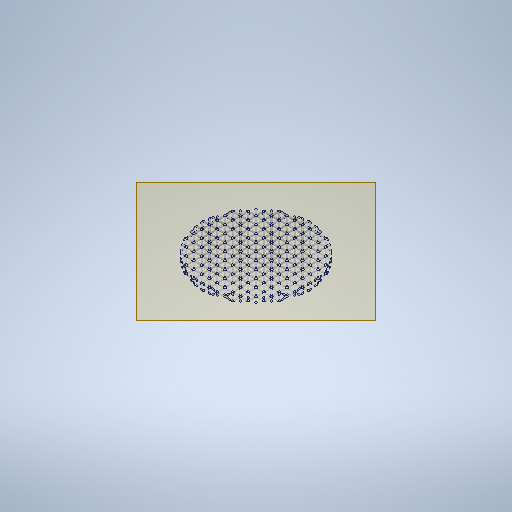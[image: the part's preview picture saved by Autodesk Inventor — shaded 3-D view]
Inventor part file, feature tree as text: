
AUTODESK INVENTOR PART (.ipt)
format: ipt  version: 2025.3 (Build 293356000, 356)  size: 2,757,632 bytes
history: native  units: in
note: dims shown in document units (in); Inventor stores cm internally (conversion verified against a paired STEP export)
features: pattern_linear x1, plane x1, extrude x1, sketch x1, other x1
ambient origin geometry x8: Origin, YZ Plane, XZ Plane, XY Plane, X Axis, Y Axis, Z Axis, Center Point
bodies: Solid1 (feature_tree)
feature tree (5):
  pattern_linear  "Rectangular Pattern1"  Count1=14 Spacing1=0.315in
  plane  "Work Plane1"
  extrude  "Extrusion1"  Depth=0.3937in
  sketch  "Sketch2"  dims[d3=5.5118in d5=0.315in d6=4.3307in d7=0.3937in d8=0.0in]
  other  "Cut-Extrude14"
